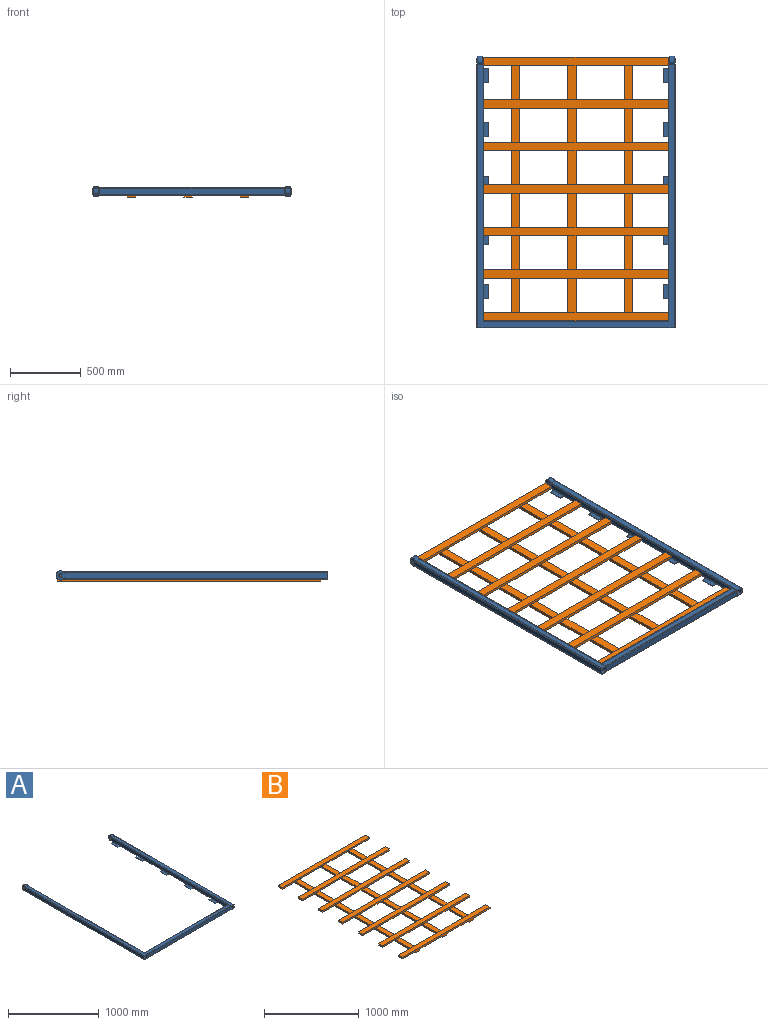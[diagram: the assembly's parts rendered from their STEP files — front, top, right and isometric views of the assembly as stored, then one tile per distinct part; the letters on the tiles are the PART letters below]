
ASSEMBLY  parts=2 mates=1
PART A: 200 faces, bbox 1400x1917.5x65 mm
  f0: cylinder r=5mm len=1855.42mm, axis (0,1,0), area 13280mm2, adj f15,f16,f18,f19,f28,f125,f126,f127
  f1: cylinder r=5mm len=1810mm, axis (0,1,0), area 10767.1mm2, adj f4,f7,f19,f59,f129,f130,f132,f134
  f2: cylinder r=5mm len=5mm, axis (0,1,0), area 14.3mm2, adj f6,f18,f60
  f3: cylinder r=5mm len=1810mm, axis (0,1,0), area 14190.7mm2, adj f4,f6,f22,f63
  f4: plane 1850x40mm, normal (-1,0,0), area 73464.2mm2, adj f1,f3,f21,f24,f25,f27,f28,f62
  f5: cylinder r=5mm len=5mm, axis (0,1,0), area 14.3mm2, adj f7,f18,f61
  f6: plane 1855x1390mm, normal (0,0,1), area 200800mm2, adj f2,f3,f8,f18,f22,f33,f34,f36
  f7: plane 1855x1390mm, normal (0,0,-1), area 258800mm2, adj f1,f5,f17,f18,f19,f31,f35,f41
  f8: cylinder r=5mm len=1855mm, axis (0,1,0), area 14569.1mm2, adj f6,f12,f18,f22
  f9: cylinder r=5mm len=1855.42mm, axis (0,1,0), area 14569.4mm2, adj f11,f13,f18,f22,f30
  f10: cylinder r=5mm len=1855.42mm, axis (0,1,0), area 14569.4mm2, adj f11,f16,f18,f22,f27
  f11: plane 1855x36mm, normal (0,0,-1), area 66780mm2, adj f9,f10,f18,f22
  f12: plane 1900x40mm, normal (1,0,0), area 75464.2mm2, adj f8,f17,f18,f20,f23,f26,f29,f30
  f13: plane 1900x36mm, normal (-1,0,0), area 67866.9mm2, adj f9,f14,f18,f20,f23,f26,f29,f30
  f14: cylinder r=5mm len=1855.42mm, axis (0,1,0), area 14569.4mm2, adj f13,f15,f18,f19,f29
  f15: plane 1855x36mm, normal (0,0,1), area 66780mm2, adj f0,f14,f18,f19
  f16: plane 1900x36mm, normal (1,0,0), area 67866.9mm2, adj f0,f10,f18,f21,f24,f25,f27,f28
  f17: cylinder r=5mm len=1855mm, axis (0,1,0), area 14569.1mm2, adj f7,f12,f18,f19
  f18: plane 1400x50mm, normal (0,-1,0), area 52768mm2, adj f0,f2,f5,f6,f7,f8,f9,f10
  f19: plane 50x5mm, normal (0,1,0), area 111.5mm2, adj f0,f1,f7,f14,f15,f17,f28,f29
  f20: plane 25x2mm, normal (0,0,-1), area 50mm2, adj f12,f13,f26,f29
  f21: plane 25x2mm, normal (0,0,-1), area 50mm2, adj f4,f16,f25,f28
  f22: plane 50x5mm, normal (0,1,0), area 111.5mm2, adj f3,f6,f8,f9,f10,f11,f27,f30
  f23: plane 25x2mm, normal (0,0,1), area 50mm2, adj f12,f13,f26,f30
  f24: plane 25x2mm, normal (0,0,1), area 50mm2, adj f4,f16,f25,f27
  f25: cylinder r=15mm len=30mm, axis (1,0,0), area 94.2mm2, adj f4,f16,f21,f24
  f26: cylinder r=15mm len=30mm, axis (-1,0,0), area 94.2mm2, adj f12,f13,f20,f23
  f27: cylinder r=5mm len=5mm, axis (-1,0,0), area 16mm2, adj f4,f10,f16,f22,f24
  f28: cylinder r=5mm len=5mm, axis (-1,0,0), area 16mm2, adj f0,f4,f16,f19,f21
  f29: cylinder r=5mm len=5mm, axis (-1,0,0), area 16mm2, adj f12,f13,f14,f19,f20
  f30: cylinder r=5mm len=5mm, axis (-1,0,0), area 16mm2, adj f9,f12,f13,f22,f23
  f31: cylinder r=5mm len=1810mm, axis (0,1,0), area 10767.1mm2, adj f7,f46,f49,f59,f84,f85,f87,f92
  f32: cylinder r=5mm len=1855.42mm, axis (0,1,0), area 13280mm2, adj f18,f42,f43,f49,f57,f80,f81,f82
  f33: cylinder r=5mm len=5mm, axis (0,1,0), area 14.3mm2, adj f6,f18,f60
  f34: cylinder r=5mm len=1810mm, axis (0,1,0), area 14190.7mm2, adj f6,f46,f52,f63
  f35: cylinder r=5mm len=5mm, axis (0,1,0), area 14.3mm2, adj f7,f18,f61
  f36: cylinder r=5mm len=1855mm, axis (0,1,0), area 14569.1mm2, adj f6,f18,f40,f52
  f37: cylinder r=5mm len=1855.42mm, axis (0,1,0), area 14569.4mm2, adj f18,f38,f45,f52,f55
  f38: plane 1855x36mm, normal (0,0,-1), area 66780mm2, adj f18,f37,f39,f52
  f39: cylinder r=5mm len=1855.42mm, axis (0,1,0), area 14569.4mm2, adj f18,f38,f42,f52,f58
  f40: plane 1900x40mm, normal (-1,0,0), area 75464.2mm2, adj f18,f36,f41,f47,f50,f53,f55,f56
  f41: cylinder r=5mm len=1855mm, axis (0,1,0), area 14569.1mm2, adj f7,f18,f40,f49
  f42: plane 1900x36mm, normal (-1,0,0), area 67866.9mm2, adj f18,f32,f39,f48,f51,f54,f57,f58
  f43: plane 1855x36mm, normal (0,0,1), area 66780mm2, adj f18,f32,f44,f49
  f44: cylinder r=5mm len=1855.42mm, axis (0,1,0), area 14569.4mm2, adj f18,f43,f45,f49,f56
  f45: plane 1900x36mm, normal (1,0,0), area 67866.9mm2, adj f18,f37,f44,f47,f50,f53,f55,f56
  f46: plane 1850x40mm, normal (1,0,0), area 73464.2mm2, adj f31,f34,f48,f51,f54,f57,f58,f62
  f47: plane 25x2mm, normal (0,0,-1), area 50mm2, adj f40,f45,f53,f56
  f48: plane 25x2mm, normal (0,0,-1), area 50mm2, adj f42,f46,f54,f57
  f49: plane 50x5mm, normal (0,1,0), area 111.5mm2, adj f7,f31,f32,f41,f43,f44,f56,f57
  f50: plane 25x2mm, normal (0,0,1), area 50mm2, adj f40,f45,f53,f55
  f51: plane 25x2mm, normal (0,0,1), area 50mm2, adj f42,f46,f54,f58
  f52: plane 50x5mm, normal (0,1,0), area 111.5mm2, adj f6,f34,f36,f37,f38,f39,f55,f58
  f53: cylinder r=15mm len=30mm, axis (1,0,0), area 94.2mm2, adj f40,f45,f47,f50
  f54: cylinder r=15mm len=30mm, axis (-1,0,0), area 94.2mm2, adj f42,f46,f48,f51
  f55: cylinder r=5mm len=5mm, axis (-1,0,0), area 16mm2, adj f37,f40,f45,f50,f52
  f56: cylinder r=5mm len=5mm, axis (-1,0,0), area 16mm2, adj f40,f44,f45,f47,f49
  f57: cylinder r=5mm len=5mm, axis (-1,0,0), area 16mm2, adj f32,f42,f46,f48,f49
  f58: cylinder r=5mm len=5mm, axis (-1,0,0), area 16mm2, adj f39,f42,f46,f51,f52
  f59: cylinder r=5mm len=1310mm, axis (-1,0,0), area 7499.8mm2, adj f1,f7,f31,f62,f64,f65,f67,f69
  f60: cylinder r=5mm len=1310mm, axis (-1,0,0), area 10238.7mm2, adj f2,f6,f18,f33
  f61: cylinder r=5mm len=1310mm, axis (-1,0,0), area 10238.7mm2, adj f5,f7,f18,f35
  f62: plane 1300x40mm, normal (0,1,0), area 52000mm2, adj f4,f46,f59,f63
  f63: cylinder r=5mm len=1310mm, axis (-1,0,0), area 10238.7mm2, adj f3,f6,f34,f62
  f64: plane 100x40.1mm, normal (0,0,1), area 4010.1mm2, adj f59,f65,f66,f67
  f65: plane 45x4mm, normal (-1,0,0), area 165.3mm2, adj f7,f59,f64,f66
  f66: plane 100x4mm, normal (0,1,0), area 400mm2, adj f7,f64,f65,f67
  f67: plane 45x4mm, normal (1,0,0), area 165.3mm2, adj f7,f59,f64,f66
  f68: plane 100x4mm, normal (0,1,0), area 400mm2, adj f7,f69,f70,f71
  f69: plane 45x4mm, normal (1,0,0), area 165.3mm2, adj f7,f59,f68,f71
  f70: plane 45x4mm, normal (-1,0,0), area 165.3mm2, adj f7,f59,f68,f71
  f71: plane 100x40.1mm, normal (0,0,1), area 4010.1mm2, adj f59,f68,f69,f70
  f72: plane 100x4mm, normal (0,1,0), area 400mm2, adj f7,f73,f74,f75
  f73: plane 45x4mm, normal (-1,0,0), area 165.3mm2, adj f7,f59,f72,f75
  f74: plane 45x4mm, normal (1,0,0), area 165.3mm2, adj f7,f59,f72,f75
  f75: plane 100x40.1mm, normal (0,0,1), area 4010.1mm2, adj f59,f72,f73,f74
  f76: plane 100x4mm, normal (0,1,0), area 400mm2, adj f7,f77,f78,f79
  f77: plane 45x4mm, normal (-1,0,0), area 165.3mm2, adj f7,f59,f76,f79
  f78: plane 45x4mm, normal (1,0,0), area 165.3mm2, adj f7,f59,f76,f79
  f79: plane 100x40.1mm, normal (0,0,1), area 4010.1mm2, adj f59,f76,f77,f78
  f80: plane 100x2mm, normal (0,0,1), area 200mm2, adj f32,f81,f82,f83
  f81: plane 2x1.58mm, normal (0,1,0), area 1.9mm2, adj f32,f80,f82
  f82: plane 100x1.58mm, normal (-1,0,0), area 158.3mm2, adj f32,f80,f81,f83
  f83: plane 2x1.58mm, normal (0,-1,0), area 1.9mm2, adj f32,f80,f82
  f84: plane 40x4mm, normal (0,-1,0), area 145.3mm2, adj f7,f31,f86,f87
  f85: plane 40x4mm, normal (0,1,0), area 145.3mm2, adj f7,f31,f86,f87
  f86: plane 100x4mm, normal (1,0,0), area 400mm2, adj f7,f84,f85,f87
  f87: plane 100x35.1mm, normal (0,0,1), area 3510.1mm2, adj f31,f84,f85,f86
  f88: plane 100x2mm, normal (0,0,1), area 200mm2, adj f32,f89,f90,f91
  f89: plane 2x1.58mm, normal (0,1,0), area 1.9mm2, adj f32,f88,f90
  f90: plane 100x1.58mm, normal (-1,0,0), area 158.3mm2, adj f32,f88,f89,f91
  f91: plane 2x1.58mm, normal (0,-1,0), area 1.9mm2, adj f32,f88,f90
  f92: plane 40x4mm, normal (0,-1,0), area 145.3mm2, adj f7,f31,f94,f95
  f93: plane 40x4mm, normal (0,1,0), area 145.3mm2, adj f7,f31,f94,f95
  f94: plane 100x4mm, normal (1,0,0), area 400mm2, adj f7,f92,f93,f95
  f95: plane 100x35.1mm, normal (0,0,1), area 3510.1mm2, adj f31,f92,f93,f94
  f96: plane 100x2mm, normal (0,0,1), area 200mm2, adj f32,f97,f98,f99
  f97: plane 2x1.58mm, normal (0,1,0), area 1.9mm2, adj f32,f96,f98
  f98: plane 100x1.58mm, normal (-1,0,0), area 158.3mm2, adj f32,f96,f97,f99
  f99: plane 2x1.58mm, normal (0,-1,0), area 1.9mm2, adj f32,f96,f98
  f100: plane 40x4mm, normal (0,-1,0), area 145.3mm2, adj f7,f31,f102,f103
  f101: plane 40x4mm, normal (0,1,0), area 145.3mm2, adj f7,f31,f102,f103
  f102: plane 100x4mm, normal (1,0,0), area 400mm2, adj f7,f100,f101,f103
  f103: plane 100x35.1mm, normal (0,0,1), area 3510.1mm2, adj f31,f100,f101,f102
  f104: plane 100x2mm, normal (0,0,1), area 200mm2, adj f32,f105,f106,f107
  f105: plane 2x1.58mm, normal (0,1,0), area 1.9mm2, adj f32,f104,f106
  f106: plane 100x1.58mm, normal (-1,0,0), area 158.3mm2, adj f32,f104,f105,f107
  f107: plane 2x1.58mm, normal (0,-1,0), area 1.9mm2, adj f32,f104,f106
  f108: plane 40x4mm, normal (0,-1,0), area 145.3mm2, adj f7,f31,f110,f111
  f109: plane 40x4mm, normal (0,1,0), area 145.3mm2, adj f7,f31,f110,f111
  f110: plane 100x4mm, normal (1,0,0), area 400mm2, adj f7,f108,f109,f111
  f111: plane 100x35.1mm, normal (0,0,1), area 3510.1mm2, adj f31,f108,f109,f110
  f112: plane 100x2mm, normal (0,0,1), area 200mm2, adj f32,f113,f114,f115
  f113: plane 2x1.58mm, normal (0,1,0), area 1.9mm2, adj f32,f112,f114
  f114: plane 100x1.58mm, normal (-1,0,0), area 158.3mm2, adj f32,f112,f113,f115
  f115: plane 2x1.58mm, normal (0,-1,0), area 1.9mm2, adj f32,f112,f114
  f116: plane 40x4mm, normal (0,-1,0), area 145.3mm2, adj f7,f31,f118,f119
  f117: plane 40x4mm, normal (0,1,0), area 145.3mm2, adj f7,f31,f118,f119
  f118: plane 100x4mm, normal (1,0,0), area 400mm2, adj f7,f116,f117,f119
  f119: plane 100x35.1mm, normal (0,0,1), area 3510.1mm2, adj f31,f116,f117,f118
  f120: cylinder r=7.5mm len=15mm, axis (-1,0,0), area 235.6mm2, adj f45,f122
  f121: plane 65x65mm, normal (1,0,0), area 3141.6mm2, adj f123,f124
  f122: plane 65x65mm, normal (-1,0,0), area 3141.6mm2, adj f120,f123
  f123: cylinder r=32.5mm len=65mm, axis (-1,0,0), area 7351.3mm2, adj f121,f122
  f124: cylinder r=7.5mm len=15mm, axis (-1,0,0), area 235.6mm2, adj f42,f121
  f125: plane 100x2mm, normal (0,0,1), area 200mm2, adj f0,f126,f127,f128
  f126: plane 100x1.58mm, normal (1,0,0), area 158.3mm2, adj f0,f125,f127,f128
  f127: plane 2x1.58mm, normal (0,1,0), area 1.9mm2, adj f0,f125,f126
  f128: plane 2x1.58mm, normal (0,-1,0), area 1.9mm2, adj f0,f125,f126
  f129: plane 100x35.1mm, normal (0,0,1), area 3510.1mm2, adj f1,f130,f131,f132
  f130: plane 40x4mm, normal (0,-1,0), area 145.3mm2, adj f1,f7,f129,f131
  f131: plane 100x4mm, normal (-1,0,0), area 400mm2, adj f7,f129,f130,f132
  f132: plane 40x4mm, normal (0,1,0), area 145.3mm2, adj f1,f7,f129,f131
  f133: plane 100x4mm, normal (-1,0,0), area 400mm2, adj f7,f134,f135,f136
  f134: plane 40x4mm, normal (0,1,0), area 145.3mm2, adj f1,f7,f133,f136
  f135: plane 40x4mm, normal (0,-1,0), area 145.3mm2, adj f1,f7,f133,f136
  f136: plane 100x35.1mm, normal (0,0,1), area 3510.1mm2, adj f1,f133,f134,f135
  f137: plane 100x1.58mm, normal (1,0,0), area 158.3mm2, adj f0,f138,f139,f140
  f138: plane 2x1.58mm, normal (0,-1,0), area 1.9mm2, adj f0,f137,f140
  f139: plane 2x1.58mm, normal (0,1,0), area 1.9mm2, adj f0,f137,f140
  f140: plane 100x2mm, normal (0,0,1), area 200mm2, adj f0,f137,f138,f139
  f141: plane 100x4mm, normal (-1,0,0), area 400mm2, adj f7,f142,f143,f144
  f142: plane 40x4mm, normal (0,-1,0), area 145.3mm2, adj f1,f7,f141,f144
  f143: plane 40x4mm, normal (0,1,0), area 145.3mm2, adj f1,f7,f141,f144
  f144: plane 100x35.1mm, normal (0,0,1), area 3510.1mm2, adj f1,f141,f142,f143
  f145: plane 2x1.58mm, normal (0,1,0), area 1.9mm2, adj f0,f146,f148
  f146: plane 100x1.58mm, normal (1,0,0), area 158.3mm2, adj f0,f145,f147,f148
  f147: plane 2x1.58mm, normal (0,-1,0), area 1.9mm2, adj f0,f146,f148
  f148: plane 100x2mm, normal (0,0,1), area 200mm2, adj f0,f145,f146,f147
  f149: plane 100x4mm, normal (-1,0,0), area 400mm2, adj f7,f150,f151,f152
  f150: plane 40x4mm, normal (0,1,0), area 145.3mm2, adj f1,f7,f149,f152
  f151: plane 40x4mm, normal (0,-1,0), area 145.3mm2, adj f1,f7,f149,f152
  f152: plane 100x35.1mm, normal (0,0,1), area 3510.1mm2, adj f1,f149,f150,f151
  f153: plane 100x1.58mm, normal (1,0,0), area 158.3mm2, adj f0,f154,f155,f156
  f154: plane 2x1.58mm, normal (0,-1,0), area 1.9mm2, adj f0,f153,f156
  f155: plane 2x1.58mm, normal (0,1,0), area 1.9mm2, adj f0,f153,f156
  f156: plane 100x2mm, normal (0,0,1), area 200mm2, adj f0,f153,f154,f155
  f157: plane 100x4mm, normal (-1,0,0), area 400mm2, adj f7,f158,f159,f160
  f158: plane 40x4mm, normal (0,1,0), area 145.3mm2, adj f1,f7,f157,f160
  f159: plane 40x4mm, normal (0,-1,0), area 145.3mm2, adj f1,f7,f157,f160
  f160: plane 100x35.1mm, normal (0,0,1), area 3510.1mm2, adj f1,f157,f158,f159
  f161: plane 100x1.58mm, normal (1,0,0), area 158.3mm2, adj f0,f162,f163,f164
  f162: plane 2x1.58mm, normal (0,-1,0), area 1.9mm2, adj f0,f161,f164
  f163: plane 2x1.58mm, normal (0,1,0), area 1.9mm2, adj f0,f161,f164
  f164: plane 100x2mm, normal (0,0,1), area 200mm2, adj f0,f161,f162,f163
  f165: cylinder r=7.5mm len=15mm, axis (1,0,0), area 235.6mm2, adj f16,f166
  f166: plane 65x65mm, normal (-1,0,0), area 3141.6mm2, adj f165,f168
  f167: plane 65x65mm, normal (1,0,0), area 3141.6mm2, adj f168,f169
  f168: cylinder r=32.5mm len=65mm, axis (1,0,0), area 7351.3mm2, adj f166,f167
  f169: cylinder r=7.5mm len=15mm, axis (1,0,0), area 235.6mm2, adj f13,f167
  f170: cylinder r=5mm len=45.17mm, axis (0,1,0), area 136.6mm2, adj f171,f192,f193,f194
  f171: plane 46x40mm, normal (-1,0,0), area 1838.9mm2, adj f170,f172,f192,f194,f195,f196,f197,f198
  f172: cylinder r=5mm len=45.17mm, axis (0,1,0), area 136.6mm2, adj f171,f197,f198,f199
  f173: cylinder r=5mm len=45.17mm, axis (0,1,0), area 136.6mm2, adj f190,f197,f198,f199
  f174: plane 2.97x1.89mm, normal (-1,0,0), area 3.6mm2, adj f175,f177,f194
  f175: plane 100x1.89mm, normal (0,-1,0), area 189.4mm2, adj f174,f176,f177,f194
  f176: plane 2.97x1.89mm, normal (1,0,0), area 3.6mm2, adj f175,f177,f194
  f177: plane 100x2.97mm, normal (0,0,1), area 297.4mm2, adj f174,f175,f176,f194
  f178: plane 2.97x1.89mm, normal (-1,0,0), area 3.6mm2, adj f179,f181,f194
  f179: plane 100x1.89mm, normal (0,-1,0), area 189.4mm2, adj f178,f180,f181,f194
  f180: plane 2.97x1.89mm, normal (1,0,0), area 3.6mm2, adj f179,f181,f194
  f181: plane 100x2.97mm, normal (0,0,1), area 297.4mm2, adj f178,f179,f180,f194
  f182: plane 100x2.97mm, normal (0,0,1), area 297.4mm2, adj f183,f184,f185,f194
  f183: plane 2.97x1.89mm, normal (-1,0,0), area 3.6mm2, adj f182,f184,f194
  f184: plane 100x1.89mm, normal (0,-1,0), area 189.4mm2, adj f182,f183,f185,f194
  f185: plane 2.97x1.89mm, normal (1,0,0), area 3.6mm2, adj f182,f184,f194
  f186: plane 100x2.97mm, normal (0,0,1), area 297.4mm2, adj f187,f188,f189,f194
  f187: plane 2.97x1.89mm, normal (-1,0,0), area 3.6mm2, adj f186,f188,f194
  f188: plane 100x1.89mm, normal (0,-1,0), area 189.4mm2, adj f186,f187,f189,f194
  f189: plane 2.97x1.89mm, normal (1,0,0), area 3.6mm2, adj f186,f188,f194
  f190: plane 46x40mm, normal (1,0,0), area 1838.9mm2, adj f173,f191,f192,f194,f195,f196,f197,f198
  f191: cylinder r=5mm len=45.17mm, axis (0,1,0), area 136.6mm2, adj f190,f192,f193,f194
  f192: cylinder r=5mm len=1302mm, axis (-1,0,0), area 10216mm2, adj f170,f171,f190,f191,f193,f195
  f193: plane 1302x36mm, normal (0,0,1), area 46872mm2, adj f170,f191,f192,f194
  f194: cylinder r=5mm len=1302mm, axis (-1,0,0), area 8774.8mm2, adj f170,f171,f174,f175,f176,f177,f178,f179
  f195: plane 1300x36mm, normal (0,1,0), area 46800mm2, adj f171,f190,f192,f197
  f196: plane 1300x36mm, normal (0,-1,0), area 46800mm2, adj f171,f190,f194,f198
  f197: cylinder r=5mm len=1302mm, axis (-1,0,0), area 10216mm2, adj f171,f172,f173,f190,f195,f199
  f198: cylinder r=5mm len=1302mm, axis (-1,0,0), area 10216mm2, adj f171,f172,f173,f190,f196,f199
  f199: plane 1302x36mm, normal (0,0,-1), area 46872mm2, adj f172,f173,f197,f198
PART B: 90 faces, bbox 1300x1860x40 mm
  f0: plane 249.1x60mm, normal (0,0,-1), area 14945.7mm2, adj f4,f6,f7,f53
  f1: plane 338x60mm, normal (0,0,-1), area 20280mm2, adj f4,f6,f70,f81
  f2: plane 338x60mm, normal (0,0,-1), area 20280mm2, adj f4,f6,f51,f83
  f3: plane 194.9x60mm, normal (0,0,-1), area 11694.3mm2, adj f4,f6,f8,f68
  f4: plane 1300x20mm, normal (0,1,0), area 26000mm2, adj f0,f1,f2,f3,f5,f7,f8,f9
  f5: plane 1300x60mm, normal (0,0,1), area 78000mm2, adj f4,f6,f7,f8
  f6: plane 1300x20mm, normal (0,-1,0), area 26000mm2, adj f0,f1,f2,f3,f5,f7,f8,f45
  f7: plane 60x20mm, normal (1,0,0), area 1200mm2, adj f0,f4,f5,f6
  f8: plane 60x20mm, normal (-1,0,0), area 1200mm2, adj f3,f4,f5,f6
  f9: plane 240x60mm, normal (0,0,1), area 14400mm2, adj f4,f18,f51,f53
  f10: plane 240x60mm, normal (0,0,1), area 14400mm2, adj f4,f18,f68,f70
  f11: plane 240x60mm, normal (0,0,1), area 14400mm2, adj f4,f18,f81,f83
  f12: plane 249.1x60mm, normal (0,0,-1), area 14945.7mm2, adj f16,f18,f19,f53
  f13: plane 338x60mm, normal (0,0,-1), area 20280mm2, adj f16,f18,f70,f81
  f14: plane 338x60mm, normal (0,0,-1), area 20280mm2, adj f16,f18,f51,f83
  f15: plane 194.9x60mm, normal (0,0,-1), area 11694.3mm2, adj f16,f18,f20,f68
  f16: plane 1300x20mm, normal (0,1,0), area 26000mm2, adj f12,f13,f14,f15,f17,f19,f20,f21
  f17: plane 1300x60mm, normal (0,0,1), area 78000mm2, adj f16,f18,f19,f20
  f18: plane 1300x20mm, normal (0,-1,0), area 26000mm2, adj f9,f10,f11,f12,f13,f14,f15,f17
  f19: plane 60x20mm, normal (1,0,0), area 1200mm2, adj f12,f16,f17,f18
  f20: plane 60x20mm, normal (-1,0,0), area 1200mm2, adj f15,f16,f17,f18
  f21: plane 240x60mm, normal (0,0,1), area 14400mm2, adj f16,f30,f51,f53
  f22: plane 240x60mm, normal (0,0,1), area 14400mm2, adj f16,f30,f68,f70
  f23: plane 240x60mm, normal (0,0,1), area 14400mm2, adj f16,f30,f81,f83
  f24: plane 249.1x60mm, normal (0,0,-1), area 14945.7mm2, adj f28,f30,f31,f53
  f25: plane 338x60mm, normal (0,0,-1), area 20280mm2, adj f28,f30,f70,f81
  f26: plane 338x60mm, normal (0,0,-1), area 20280mm2, adj f28,f30,f51,f83
  f27: plane 194.9x60mm, normal (0,0,-1), area 11694.3mm2, adj f28,f30,f32,f68
  f28: plane 1300x20mm, normal (0,1,0), area 26000mm2, adj f24,f25,f26,f27,f29,f31,f32,f33
  f29: plane 1300x60mm, normal (0,0,1), area 78000mm2, adj f28,f30,f31,f32
  f30: plane 1300x20mm, normal (0,-1,0), area 26000mm2, adj f21,f22,f23,f24,f25,f26,f27,f29
  f31: plane 60x20mm, normal (1,0,0), area 1200mm2, adj f24,f28,f29,f30
  f32: plane 60x20mm, normal (-1,0,0), area 1200mm2, adj f27,f28,f29,f30
  f33: plane 240x60mm, normal (0,0,1), area 14400mm2, adj f28,f51,f53,f77
  f34: plane 240x60mm, normal (0,0,1), area 14400mm2, adj f28,f68,f70,f77
  f35: plane 240x60mm, normal (0,0,1), area 14400mm2, adj f28,f77,f81,f83
  f36: plane 249.1x60mm, normal (0,0,-1), area 14945.7mm2, adj f40,f42,f43,f53
  f37: plane 338x60mm, normal (0,0,-1), area 20280mm2, adj f40,f42,f70,f81
  f38: plane 338x60mm, normal (0,0,-1), area 20280mm2, adj f40,f42,f51,f83
  f39: plane 194.9x60mm, normal (0,0,-1), area 11694.3mm2, adj f40,f42,f44,f68
  f40: plane 1300x20mm, normal (0,1,0), area 26000mm2, adj f36,f37,f38,f39,f41,f43,f44,f45
  f41: plane 1300x60mm, normal (0,0,1), area 78000mm2, adj f40,f42,f43,f44
  f42: plane 1300x40mm, normal (0,-1,0), area 29600mm2, adj f36,f37,f38,f39,f41,f43,f44,f51
  f43: plane 60x20mm, normal (1,0,0), area 1200mm2, adj f36,f40,f41,f42
  f44: plane 60x20mm, normal (-1,0,0), area 1200mm2, adj f39,f40,f41,f42
  f45: plane 240x60mm, normal (0,0,1), area 14400mm2, adj f6,f40,f51,f53
  f46: plane 240x60mm, normal (0,0,1), area 14400mm2, adj f6,f40,f68,f70
  f47: plane 240x60mm, normal (0,0,1), area 14400mm2, adj f6,f40,f81,f83
  f48: plane 240x60mm, normal (0,0,1), area 14400mm2, adj f51,f53,f62,f75
  f49: plane 240x60mm, normal (0,0,1), area 14400mm2, adj f51,f53,f60,f87
  f50: plane 1300x40mm, normal (0,1,0), area 29600mm2, adj f51,f52,f53,f56,f68,f69,f70,f72
  f51: plane 1860x20mm, normal (-1,0,0), area 37200mm2, adj f2,f9,f14,f21,f26,f33,f38,f42
  f52: plane 1860x60mm, normal (0,0,-1), area 111600mm2, adj f42,f50,f51,f53
  f53: plane 1860x20mm, normal (1,0,0), area 37200mm2, adj f0,f9,f12,f21,f24,f33,f36,f42
  f54: plane 338x60mm, normal (0,0,-1), area 20280mm2, adj f51,f60,f62,f83
  f55: plane 338x60mm, normal (0,0,-1), area 20280mm2, adj f51,f75,f77,f83
  f56: plane 338x60mm, normal (0,0,-1), area 20280mm2, adj f50,f51,f83,f87
  f57: plane 338x60mm, normal (0,0,-1), area 20280mm2, adj f60,f62,f70,f81
  f58: plane 249.1x60mm, normal (0,0,-1), area 14945.7mm2, adj f53,f60,f62,f63
  f59: plane 194.9x60mm, normal (0,0,-1), area 11694.3mm2, adj f60,f62,f64,f68
  f60: plane 1300x20mm, normal (0,1,0), area 26000mm2, adj f49,f54,f57,f58,f59,f61,f63,f64
  f61: plane 1300x60mm, normal (0,0,1), area 78000mm2, adj f60,f62,f63,f64
  f62: plane 1300x20mm, normal (0,-1,0), area 26000mm2, adj f48,f54,f57,f58,f59,f61,f63,f64
  f63: plane 60x20mm, normal (1,0,0), area 1200mm2, adj f58,f60,f61,f62
  f64: plane 60x20mm, normal (-1,0,0), area 1200mm2, adj f59,f60,f61,f62
  f65: plane 240x60mm, normal (0,0,1), area 14400mm2, adj f60,f68,f70,f87
  f66: plane 240x60mm, normal (0,0,1), area 14400mm2, adj f60,f81,f83,f87
  f67: plane 240x60mm, normal (0,0,1), area 14400mm2, adj f62,f68,f70,f75
  f68: plane 1860x20mm, normal (-1,0,0), area 37200mm2, adj f3,f10,f15,f22,f27,f34,f39,f42
  f69: plane 1860x60mm, normal (0,0,-1), area 111600mm2, adj f42,f50,f68,f70
  f70: plane 1860x20mm, normal (1,0,0), area 37200mm2, adj f1,f10,f13,f22,f25,f34,f37,f42
  f71: plane 194.9x60mm, normal (0,0,-1), area 11694.3mm2, adj f68,f75,f77,f79
  f72: plane 194.9x60mm, normal (0,0,-1), area 11694.3mm2, adj f50,f68,f87,f89
  f73: plane 249.1x60mm, normal (0,0,-1), area 14945.7mm2, adj f53,f75,f77,f78
  f74: plane 338x60mm, normal (0,0,-1), area 20280mm2, adj f70,f75,f77,f81
  f75: plane 1300x20mm, normal (0,1,0), area 26000mm2, adj f48,f55,f67,f71,f73,f74,f76,f78
  f76: plane 1300x60mm, normal (0,0,1), area 78000mm2, adj f75,f77,f78,f79
  f77: plane 1300x20mm, normal (0,-1,0), area 26000mm2, adj f33,f34,f35,f55,f71,f73,f74,f76
  f78: plane 60x20mm, normal (1,0,0), area 1200mm2, adj f73,f75,f76,f77
  f79: plane 60x20mm, normal (-1,0,0), area 1200mm2, adj f71,f75,f76,f77
  f80: plane 240x60mm, normal (0,0,1), area 14400mm2, adj f62,f75,f81,f83
  f81: plane 1860x20mm, normal (-1,0,0), area 37200mm2, adj f1,f11,f13,f23,f25,f35,f37,f42
  f82: plane 1860x60mm, normal (0,0,-1), area 111600mm2, adj f42,f50,f81,f83
  f83: plane 1860x20mm, normal (1,0,0), area 37200mm2, adj f2,f11,f14,f23,f26,f35,f38,f42
  f84: plane 338x60mm, normal (0,0,-1), area 20280mm2, adj f50,f70,f81,f87
  f85: plane 249.1x60mm, normal (0,0,-1), area 14945.7mm2, adj f50,f53,f87,f88
  f86: plane 1300x60mm, normal (0,0,1), area 78000mm2, adj f50,f87,f88,f89
  f87: plane 1300x20mm, normal (0,-1,0), area 26000mm2, adj f49,f56,f65,f66,f72,f84,f85,f86
  f88: plane 60x20mm, normal (1,0,0), area 1200mm2, adj f50,f85,f86,f87
  f89: plane 60x20mm, normal (-1,0,0), area 1200mm2, adj f50,f72,f86,f87
PLACE A at identity
PLACE B t=(-650,-1790,-20)mm
MATE fastened B.f42 <-> A.f62  axis (0,-1,0) through (-650,-1850,-20)mm
